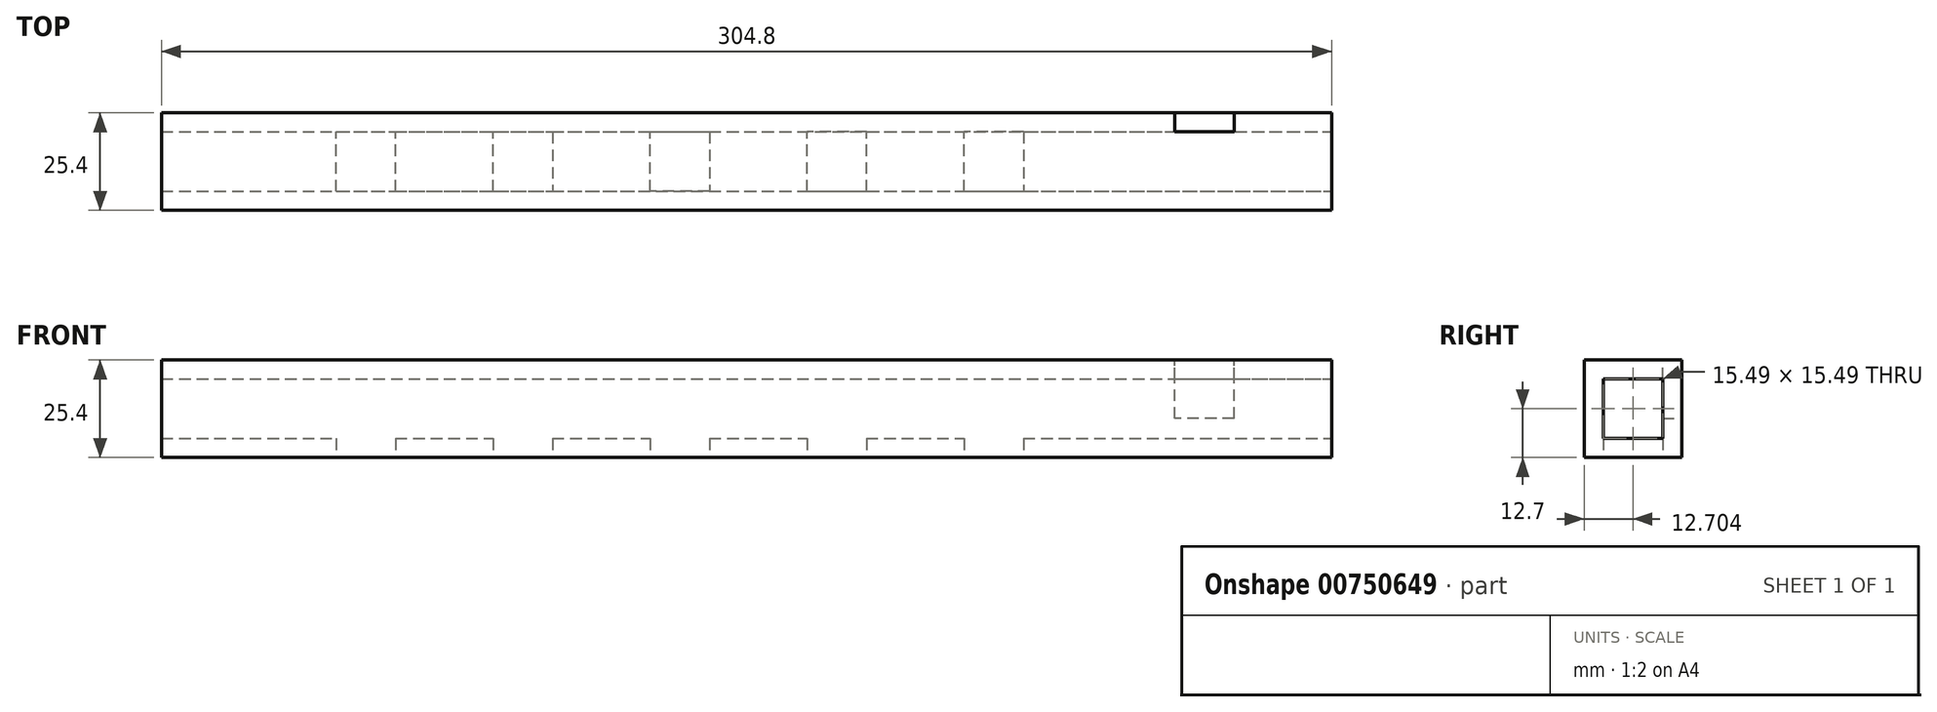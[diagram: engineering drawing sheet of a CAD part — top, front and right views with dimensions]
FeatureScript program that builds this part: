
annotation { "Feature Type Name" : "Feature", "Feature Type Description" : "" }
export const myFeature = defineFeature(function(context is Context, id is Id, definition is map)
    precondition{}
    {
        {
            var Q0;
            Q0=qCreatedBy(makeId("Right.planeOp"),FACE);
            var sketch = newSketch(context, id + "F0", { "sketchPlane" : qUnion([Q0])});
            skLineSegment(sketch, "E0.bottom", {"start": v(-15.86, 25.4) * mm, "end": v(9.54, 25.4) * mm});
            skLineSegment(sketch, "E0.top", {"start": v(-15.86, 0) * mm, "end": v(9.54, 0) * mm});
            skLineSegment(sketch, "E0.left", {"start": v(-15.86, 25.4) * mm, "end": v(-15.86, 0) * mm});
            skLineSegment(sketch, "E0.right", {"start": v(9.54, 25.4) * mm, "end": v(9.54, 0) * mm});
            skSolve(sketch);
        }
        {
            var Q0;
            Q0=makeQuery(id+"F0.imprint","IMPRINT",FACE,{"disambiguationData":[TD([[makeQuery(id+"F0.imprint","IMPRINT",EDGE,{"derivedFrom":sQuery(id+"F0.wireOp",EDGE,"E0.bottom")}),-1.0]])]});
            extrude(context, id + "F1", {"entities" : qUnion([Q0]), "oppositeDirection" : true, "depth" : 152.4 * mm, "offsetDistance" : 25.4 * mm});
        }
        {
            var Q0;
            Q0=makeQuery(id+"F1.opExtrude","CAP_FACE",FACE,{"disambiguationData":[OSD([sQuery(id+"F0.wireOp",EDGE,"E0.bottom"),sQuery(id+"F0.wireOp",EDGE,"E0.top"),sQuery(id+"F0.wireOp",EDGE,"E0.left"),sQuery(id+"F0.wireOp",EDGE,"E0.right")])],"isStart":true});
            extrude(context, id + "F2", {"entities" : qUnion([Q0]), "operationType" : NewBodyOperationType.ADD, "depth" : 152.4 * mm, "offsetDistance" : 25.4 * mm});
        }
        {
            var Q0;
            Q0=makeQuery(id+"F2.opExtrude","CAP_FACE",FACE,{"disambiguationData":[OSD([sQuery(id+"F0.wireOp",EDGE,"E0.bottom"),sQuery(id+"F0.wireOp",EDGE,"E0.top"),sQuery(id+"F0.wireOp",EDGE,"E0.left"),sQuery(id+"F0.wireOp",EDGE,"E0.right")])],"isStart":false});
            var sketch = newSketch(context, id + "F3", { "sketchPlane" : qUnion([Q0])});
            skLineSegment(sketch, "E1.bottom", {"start": v(-10.9, 20.45) * mm, "end": v(4.6, 20.45) * mm});
            skLineSegment(sketch, "E1.top", {"start": v(-10.9, 4.95) * mm, "end": v(4.6, 4.95) * mm});
            skLineSegment(sketch, "E1.left", {"start": v(-10.9, 20.45) * mm, "end": v(-10.9, 4.95) * mm});
            skLineSegment(sketch, "E1.right", {"start": v(4.6, 20.45) * mm, "end": v(4.6, 4.95) * mm});
            skSolve(sketch);
        }
        {
            var Q0;
            Q0=makeQuery(id+"F3.imprint","IMPRINT",FACE,{"disambiguationData":[TD([[makeQuery(id+"F3.imprint","IMPRINT",EDGE,{"derivedFrom":sQuery(id+"F3.wireOp",EDGE,"E1.bottom")}),-1.0]])]});
            extrude(context, id + "F4", {"entities" : qUnion([Q0]), "operationType" : NewBodyOperationType.REMOVE, "endBound" : BoundingType.THROUGH_ALL, "oppositeDirection" : true, "depth" : 25.4 * mm, "offsetDistance" : 25.4 * mm});
        }
        {
            var Q0;
            {var subQ0=sQuery(id+"F0.wireOp",EDGE,"E0.top");Q0=makeQuery(id+"F2.boolean.opBoolean","MERGE",FACE,{"derivedFrom":[makeQuery(id+"F1.opExtrude","SWEPT_FACE",FACE,{"disambiguationData":[OSD([subQ0])]}),makeQuery(id+"F2.opExtrude","SWEPT_FACE",FACE,{"disambiguationData":[OSD([subQ0])]})]});}
            var sketch = newSketch(context, id + "F5", { "sketchPlane" : qUnion([Q0])});
            skLineSegment(sketch, "E2.bottom", {"start": v(-106.93, 10.9) * mm, "end": v(-91.44, 10.9) * mm});
            skLineSegment(sketch, "E2.top", {"start": v(-106.93, -4.6) * mm, "end": v(-91.44, -4.6) * mm});
            skLineSegment(sketch, "E2.left", {"start": v(-106.93, 10.9) * mm, "end": v(-106.93, -4.6) * mm});
            skLineSegment(sketch, "E2.right", {"start": v(-91.44, 10.9) * mm, "end": v(-91.44, -4.6) * mm});
            skLineSegment(sketch, "E3.bottom", {"start": v(-45.97, 10.9) * mm, "end": v(-30.48, 10.9) * mm});
            skLineSegment(sketch, "E3.top", {"start": v(-45.97, -4.6) * mm, "end": v(-30.48, -4.6) * mm});
            skLineSegment(sketch, "E3.left", {"start": v(-45.97, 10.9) * mm, "end": v(-45.97, -4.6) * mm});
            skLineSegment(sketch, "E3.right", {"start": v(-30.48, 10.9) * mm, "end": v(-30.48, -4.6) * mm});
            skLineSegment(sketch, "E4.bottom", {"start": v(14.99, 10.9) * mm, "end": v(30.48, 10.9) * mm});
            skLineSegment(sketch, "E4.top", {"start": v(14.99, -4.6) * mm, "end": v(30.48, -4.6) * mm});
            skLineSegment(sketch, "E4.left", {"start": v(14.99, 10.9) * mm, "end": v(14.99, -4.6) * mm});
            skLineSegment(sketch, "E4.right", {"start": v(30.48, 10.9) * mm, "end": v(30.48, -4.6) * mm});
            skLineSegment(sketch, "E5.bottom", {"start": v(75.95, 10.9) * mm, "end": v(91.44, 10.9) * mm});
            skLineSegment(sketch, "E5.top", {"start": v(75.95, -4.6) * mm, "end": v(91.44, -4.6) * mm});
            skLineSegment(sketch, "E5.left", {"start": v(75.95, 10.9) * mm, "end": v(75.95, -4.6) * mm});
            skLineSegment(sketch, "E5.right", {"start": v(91.44, 10.9) * mm, "end": v(91.44, -4.6) * mm});
            skSolve(sketch);
        }
        {
            var Q0;
            Q0=makeQuery(id+"F5.imprint","IMPRINT",FACE,{"disambiguationData":[TD([[makeQuery(id+"F5.imprint","IMPRINT",EDGE,{"derivedFrom":sQuery(id+"F5.wireOp",EDGE,"E2.bottom")}),-1.0]])]});
            extrude(context, id + "F6", {"entities" : qUnion([Q0]), "operationType" : NewBodyOperationType.REMOVE, "oppositeDirection" : true, "depth" : 19.05 * mm, "offsetDistance" : 25.4 * mm});
        }
        {
            var Q0;
            {var subQ0=sQuery(id+"F0.wireOp",EDGE,"E0.top");Q0=makeQuery(id+"F2.boolean.opBoolean","MERGE",FACE,{"derivedFrom":[makeQuery(id+"F1.opExtrude","SWEPT_FACE",FACE,{"disambiguationData":[OSD([subQ0])]}),makeQuery(id+"F2.opExtrude","SWEPT_FACE",FACE,{"disambiguationData":[OSD([subQ0])]})]});}
            var sketch = newSketch(context, id + "F7", { "sketchPlane" : qUnion([Q0])});
            skLineSegment(sketch, "E6", {"start": v(-106.93, -4.6) * mm, "end": v(-106.93, -9.54) * mm});
            skLineSegment(sketch, "E7", {"start": v(-106.93, 10.9) * mm, "end": v(-106.93, 15.86) * mm});
            skLineSegment(sketch, "E8", {"start": v(-106.93, -4.6) * mm, "end": v(-152.4, -4.6) * mm});
            skLineSegment(sketch, "E9", {"start": v(-91.44, -4.6) * mm, "end": v(-66.04, -4.6) * mm});
            skLineSegment(sketch, "E10", {"start": v(-91.44, 10.9) * mm, "end": v(-66.04, 10.9) * mm});
            skLineSegment(sketch, "E11", {"start": v(-66.04, -4.6) * mm, "end": v(-50.55, -4.6) * mm});
            skLineSegment(sketch, "E12", {"start": v(-66.04, 10.9) * mm, "end": v(-50.55, 10.9) * mm});
            skLineSegment(sketch, "E13", {"start": v(-50.55, -4.6) * mm, "end": v(-50.55, 10.9) * mm});
            skLineSegment(sketch, "E14", {"start": v(-50.55, 10.9) * mm, "end": v(-25.15, 10.9) * mm});
            skLineSegment(sketch, "E15", {"start": v(-50.55, -4.6) * mm, "end": v(-25.15, -4.6) * mm});
            skLineSegment(sketch, "E16", {"start": v(-25.15, 10.9) * mm, "end": v(-25.15, -4.6) * mm});
            skLineSegment(sketch, "E17", {"start": v(-25.15, -4.6) * mm, "end": v(-9.65, -4.6) * mm});
            skLineSegment(sketch, "E18", {"start": v(-9.65, -4.6) * mm, "end": v(-9.65, 10.9) * mm});
            skLineSegment(sketch, "E19", {"start": v(-9.65, 10.9) * mm, "end": v(-25.15, 10.9) * mm});
            skLineSegment(sketch, "E20", {"start": v(-9.65, 10.9) * mm, "end": v(15.75, 10.9) * mm});
            skLineSegment(sketch, "E21", {"start": v(-9.65, -4.6) * mm, "end": v(15.75, -4.6) * mm});
            skLineSegment(sketch, "E22", {"start": v(15.75, 10.9) * mm, "end": v(15.75, -4.6) * mm});
            skLineSegment(sketch, "E23", {"start": v(15.75, 10.9) * mm, "end": v(31.24, 10.9) * mm});
            skLineSegment(sketch, "E24", {"start": v(31.24, 10.9) * mm, "end": v(31.24, -4.6) * mm});
            skLineSegment(sketch, "E25", {"start": v(31.24, -4.6) * mm, "end": v(15.75, -4.6) * mm});
            skLineSegment(sketch, "E26", {"start": v(31.24, 10.9) * mm, "end": v(56.64, 10.9) * mm});
            skLineSegment(sketch, "E27", {"start": v(31.24, -4.6) * mm, "end": v(56.64, -4.6) * mm});
            skLineSegment(sketch, "E28", {"start": v(56.64, 10.9) * mm, "end": v(56.64, -4.6) * mm});
            skLineSegment(sketch, "E29", {"start": v(72.14, -4.6) * mm, "end": v(56.64, -4.6) * mm});
            skLineSegment(sketch, "E30", {"start": v(72.14, -4.6) * mm, "end": v(72.14, 10.9) * mm});
            skLineSegment(sketch, "E31", {"start": v(56.64, 10.9) * mm, "end": v(72.14, 10.9) * mm});
            skLineSegment(sketch, "E32", {"start": v(-66.04, 10.9) * mm, "end": v(-66.04, -4.6) * mm});
            skSolve(sketch);
        }
        {
            var Q0;
            Q0=makeQuery(id+"F7.imprint","IMPRINT",FACE,{"disambiguationData":[TD([[makeQuery(id+"F7.imprint","IMPRINT",EDGE,{"derivedFrom":sQuery(id+"F7.wireOp",EDGE,"E11")}),1.0]])]});
            extrude(context, id + "F8", {"entities" : qUnion([Q0]), "operationType" : NewBodyOperationType.REMOVE, "oppositeDirection" : true, "depth" : 17.78 * mm, "offsetDistance" : 25.4 * mm});
        }
        {
            var Q0;
            Q0=makeQuery(id+"F7.imprint","IMPRINT",FACE,{"disambiguationData":[TD([[makeQuery(id+"F7.imprint","IMPRINT",EDGE,{"derivedFrom":sQuery(id+"F7.wireOp",EDGE,"E16")}),1.0]])]});
            extrude(context, id + "F9", {"entities" : qUnion([Q0]), "operationType" : NewBodyOperationType.REMOVE, "oppositeDirection" : true, "depth" : 15.24 * mm, "offsetDistance" : 25.4 * mm});
        }
        {
            var Q0;
            Q0=makeQuery(id+"F7.imprint","IMPRINT",FACE,{"disambiguationData":[TD([[makeQuery(id+"F7.imprint","IMPRINT",EDGE,{"derivedFrom":sQuery(id+"F7.wireOp",EDGE,"E22")}),1.0]])]});
            extrude(context, id + "F10", {"entities" : qUnion([Q0]), "operationType" : NewBodyOperationType.REMOVE, "oppositeDirection" : true, "depth" : 15.24 * mm, "offsetDistance" : 25.4 * mm});
        }
        {
            var Q0;
            Q0=makeQuery(id+"F7.imprint","IMPRINT",FACE,{"disambiguationData":[TD([[makeQuery(id+"F7.imprint","IMPRINT",EDGE,{"derivedFrom":sQuery(id+"F7.wireOp",EDGE,"E28")}),1.0]])]});
            extrude(context, id + "F11", {"entities" : qUnion([Q0]), "operationType" : NewBodyOperationType.REMOVE, "oppositeDirection" : true, "depth" : 15.24 * mm, "offsetDistance" : 25.4 * mm});
        }
        {
            var Q0;
            {var subQ0=sQuery(id+"F0.wireOp",EDGE,"E0.bottom");Q0=makeQuery(id+"F2.boolean.opBoolean","MERGE",FACE,{"derivedFrom":[makeQuery(id+"F1.opExtrude","SWEPT_FACE",FACE,{"disambiguationData":[OSD([subQ0])]}),makeQuery(id+"F2.opExtrude","SWEPT_FACE",FACE,{"disambiguationData":[OSD([subQ0])]})]});}
            var sketch = newSketch(context, id + "F12", { "sketchPlane" : qUnion([Q0])});
            skLineSegment(sketch, "E33", {"start": v(152.4, -3.16) * mm, "end": v(127, -3.16) * mm});
            skLineSegment(sketch, "E34", {"start": v(127, -3.16) * mm, "end": v(127, 9.54) * mm});
            skLineSegment(sketch, "E35", {"start": v(127, -3.16) * mm, "end": v(127, -15.86) * mm});
            skLineSegment(sketch, "E36", {"start": v(127, -15.86) * mm, "end": v(111.5, -15.86) * mm});
            skLineSegment(sketch, "E37", {"start": v(127, 9.54) * mm, "end": v(111.5, 9.54) * mm});
            skLineSegment(sketch, "E38", {"start": v(111.5, -15.86) * mm, "end": v(111.5, 9.54) * mm});
            skLineSegment(sketch, "E39", {"start": v(127, 9.54) * mm, "end": v(127, 4.6) * mm});
            skLineSegment(sketch, "E40", {"start": v(127, 4.6) * mm, "end": v(111.5, 4.6) * mm});
            skLineSegment(sketch, "E41", {"start": v(127, -3.16) * mm, "end": v(127, -10.9) * mm});
            skLineSegment(sketch, "E42", {"start": v(127, -10.9) * mm, "end": v(111.5, -10.9) * mm});
            skLineSegment(sketch, "E43", {"start": v(111.5, -10.9) * mm, "end": v(111.5, 4.6) * mm});
            skSolve(sketch);
        }
        {
            var Q0;
            Q0=makeQuery(id+"F12.imprint","IMPRINT",FACE,{"disambiguationData":[TD([[makeQuery(id+"F12.imprint","IMPRINT",EDGE,{"derivedFrom":sQuery(id+"F12.wireOp",EDGE,"E34")}),1.0]])]});
            extrude(context, id + "F13", {"entities" : qUnion([Q0]), "operationType" : NewBodyOperationType.REMOVE, "oppositeDirection" : true, "depth" : 15.24 * mm, "offsetDistance" : 25.4 * mm});
        }
    });
